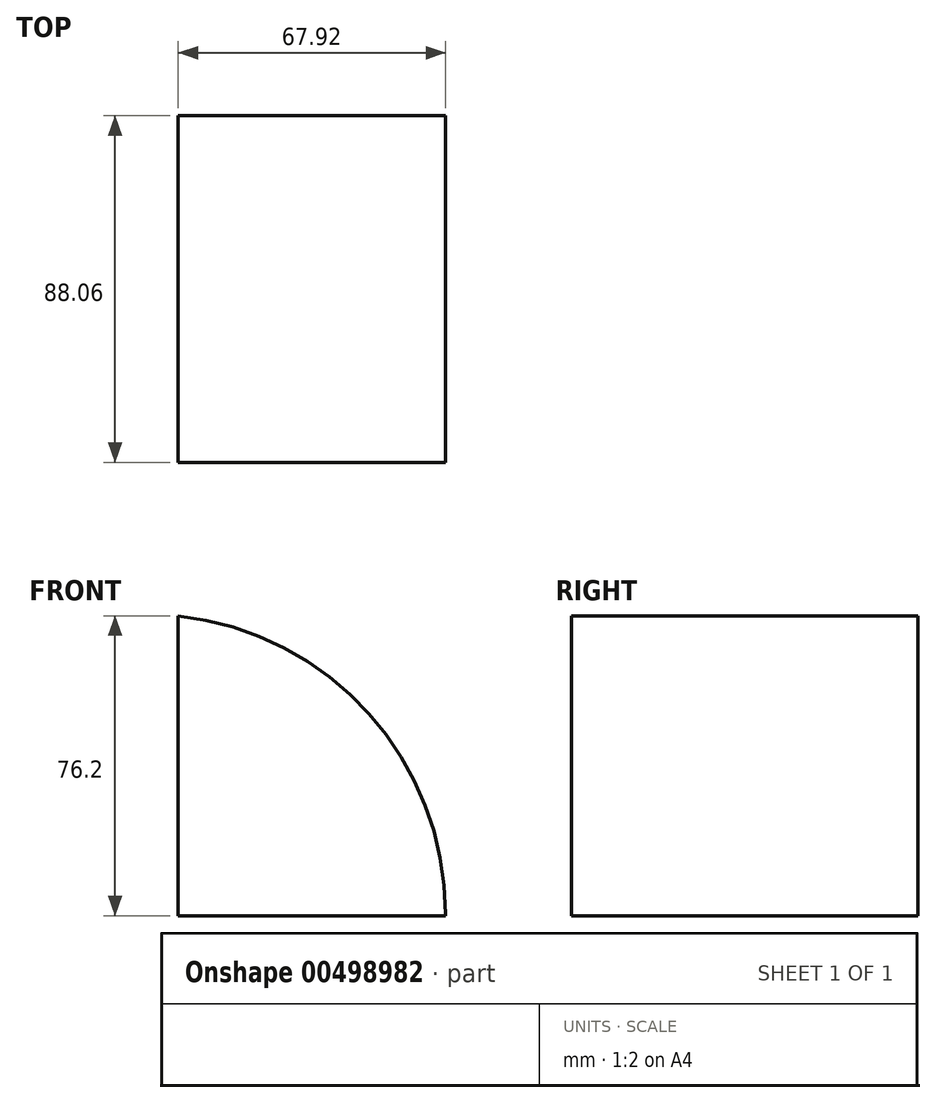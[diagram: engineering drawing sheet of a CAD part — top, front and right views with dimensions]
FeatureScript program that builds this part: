
annotation { "Feature Type Name" : "Feature", "Feature Type Description" : "" }
export const myFeature = defineFeature(function(context is Context, id is Id, definition is map)
    precondition{}
    {
        {
            var Q0;
            Q0=qCreatedBy(makeId("Top.planeOp"),FACE);
            var sketch = newSketch(context, id + "F0", { "sketchPlane" : qUnion([Q0])});
            skLineSegment(sketch, "E0.bottom", {"start": v(33.96, 44.03) * mm, "end": v(-33.96, 44.03) * mm});
            skLineSegment(sketch, "E0.top", {"start": v(33.96, -44.03) * mm, "end": v(-33.96, -44.03) * mm});
            skLineSegment(sketch, "E0.left", {"start": v(33.96, 44.03) * mm, "end": v(33.96, -44.03) * mm});
            skLineSegment(sketch, "E0.right", {"start": v(-33.96, 44.03) * mm, "end": v(-33.96, -44.03) * mm});
            skPoint(sketch, "E0.middle", {"position": v(0, 0) * mm});
            skSolve(sketch);
        }
        {
            var Q0;
            Q0=makeQuery(id+"F0.imprint","IMPRINT",FACE,{"disambiguationData":[TD([[makeQuery(id+"F0.imprint","IMPRINT",EDGE,{"derivedFrom":sQuery(id+"F0.wireOp",EDGE,"E0.bottom")}),1.0]])]});
            extrude(context, id + "F1", {"entities" : qUnion([Q0]), "depth" : 76.2 * mm});
        }
        {
            var Q0;
            Q0=makeQuery(id+"F1.opExtrude","CAP_EDGE",EDGE,{"disambiguationData":[OSD([sQuery(id+"F0.wireOp",EDGE,"E0.left")])],"isStart":false});
            fillet(context, id + "F2", {"entities" : qUnion([Q0]), "radius" : 76.2 * mm, "tangentPropagation" : true, "allowEdgeOverflow" : false});
        }
    });
